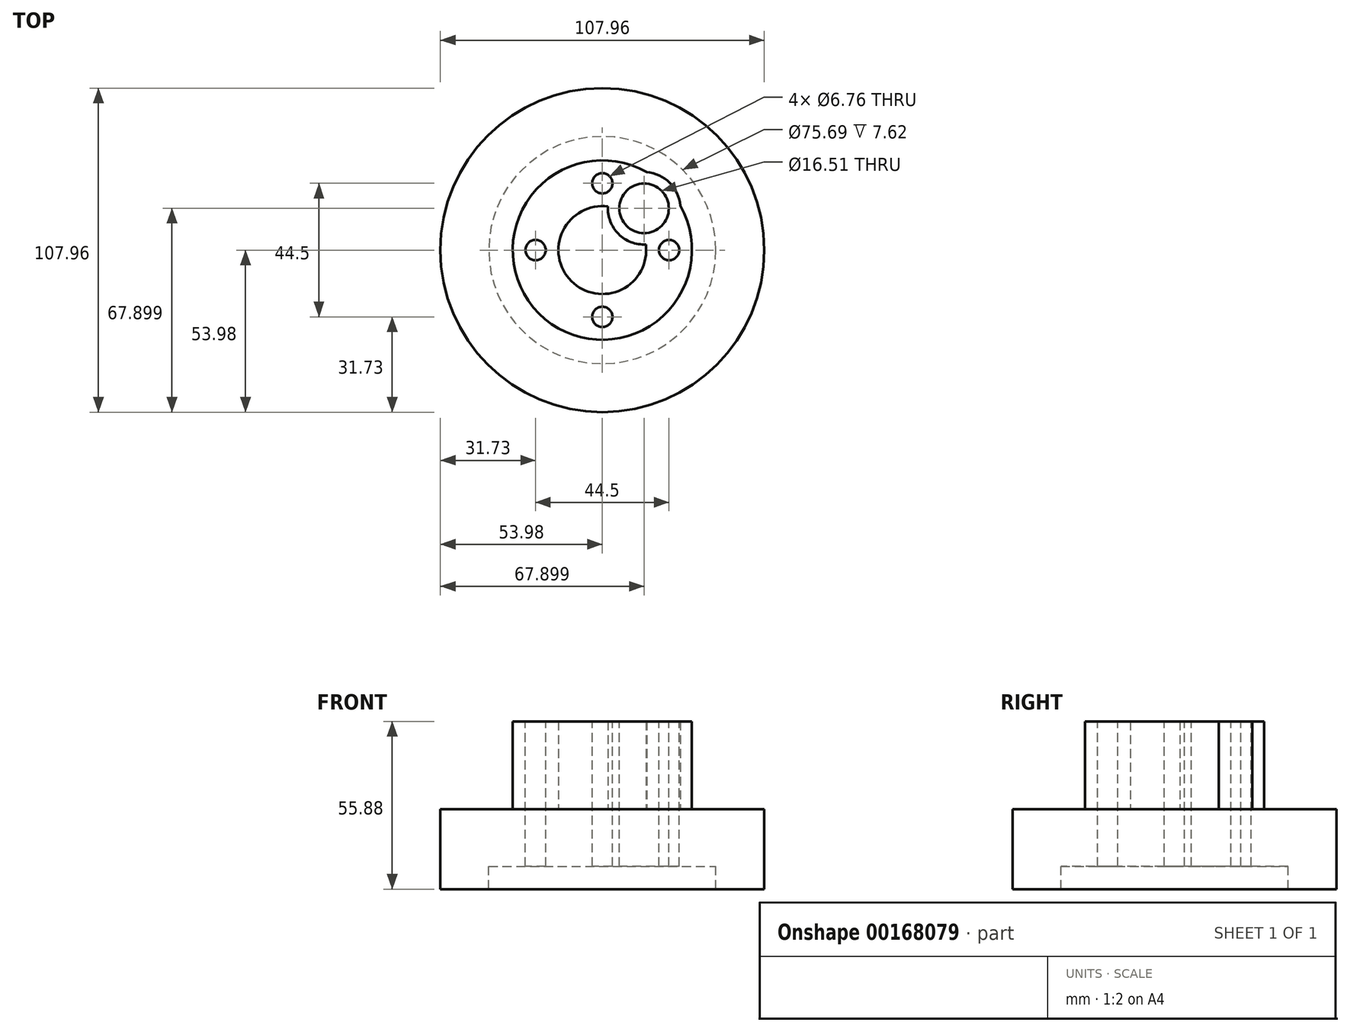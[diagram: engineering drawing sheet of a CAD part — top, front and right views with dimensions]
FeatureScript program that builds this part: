
annotation { "Feature Type Name" : "Feature", "Feature Type Description" : "" }
export const myFeature = defineFeature(function(context is Context, id is Id, definition is map)
    precondition{}
    {
        {
            var Q0;
            Q0=qCreatedBy(makeId("Top.planeOp"),FACE);
            var sketch = newSketch(context, id + "F0", { "sketchPlane" : qUnion([Q0])});
            skCircle(sketch, "E0", {"center": v(0, 0) * mm, "radius": 53.98 * mm});
            skSolve(sketch);
        }
        {
            var Q0;
            Q0=qSketchRegion(id+"F0",true);
            extrude(context, id + "F1", {"entities" : qUnion([Q0]), "depth" : 19.05 * mm});
        }
        {
            var Q0;
            Q0=makeQuery(id+"F1.opExtrude","CAP_FACE",FACE,{"disambiguationData":[OSD([sQuery(id+"F0.wireOp",EDGE,"E0")])],"isStart":false});
            var sketch = newSketch(context, id + "F2", { "sketchPlane" : qUnion([Q0])});
            skCircle(sketch, "E1", {"center": v(0, 0) * mm, "radius": 22.25 * mm, "construction": true});
            skCircle(sketch, "E2", {"center": v(0, 0) * mm, "radius": 14.63 * mm});
            skCircle(sketch, "E3", {"center": v(0, 0) * mm, "radius": 29.87 * mm});
            skSolve(sketch);
        }
        {
            var Q0;
            Q0=qSketchRegion(id+"F2",true);
            var Q1;
            Q1=qConstructionFilter(qBodyType(qCreatedBy(id+"F2",EDGE),BodyType.WIRE),ConstructionObject.NO);
            extrude(context, id + "F3", {"entities" : qUnion([Q0]), "operationType" : NewBodyOperationType.ADD, "surfaceEntities" : qUnion([Q1]), "depth" : 29.2 * mm});
        }
        {
            var Q0;
            Q0=makeQuery(id+"F3.opExtrude","CAP_FACE",FACE,{"disambiguationData":[OSD([sQuery(id+"F2.wireOp",EDGE,"E2"),sQuery(id+"F2.wireOp",EDGE,"E3")])],"isStart":false});
            var sketch = newSketch(context, id + "F4", { "sketchPlane" : qUnion([Q0])});
            skPoint(sketch, "E4", {"position": v(0, -22.25) * mm});
            skPoint(sketch, "E5", {"position": v(-22.25, 0) * mm});
            skPoint(sketch, "E6", {"position": v(0, 22.25) * mm});
            skPoint(sketch, "E7", {"position": v(22.25, 0) * mm});
            skLineSegment(sketch, "E8", {"start": v(-14.63, 0) * mm, "end": v(-29.87, 0) * mm, "construction": true});
            skLineSegment(sketch, "E9", {"start": v(0, -14.63) * mm, "end": v(0, -29.87) * mm, "construction": true});
            skLineSegment(sketch, "E10", {"start": v(14.63, 0) * mm, "end": v(29.87, 0) * mm, "construction": true});
            skLineSegment(sketch, "E11", {"start": v(0, 14.63) * mm, "end": v(0, 29.87) * mm, "construction": true});
            skSolve(sketch);
        }
        {
            var Q0;
            Q0=sQuery(id+"F4.wireOp",VERTEX,"E4");
            var Q1;
            Q1=sQuery(id+"F4.wireOp",VERTEX,"E5");
            var Q2;
            Q2=sQuery(id+"F4.wireOp",VERTEX,"E6");
            var Q3;
            Q3=sQuery(id+"F4.wireOp",VERTEX,"E7");
            var Q4;
            Q4=makeQuery(id+"F1.opExtrude","SWEPT_BODY",BODY,{"disambiguationData":[OSD([sQuery(id+"F0.wireOp",EDGE,"E0")])]});
            hole(context, id + "F5", {"style" : HoleStyle.SIMPLE, "endStyle" : HoleEndStyle.THROUGH, "standardTappedOrClearance" : lookupTablePath({ "standard" : "ANSI", "fit" : "Normal (ASME)", "size" : "1/4", "type" : "Clearance" }), "standardBlindInLast" : lookupTablePath({ "fit" : "Free", "standard" : "ANSI", "size" : "1/4", "type" : "Clearance" }), "holeDiameter" : 6.76 * mm, "locations" : qUnion([Q0, Q1, Q2, Q3]), "scope" : qUnion([Q4]), "isTappedThrough" : true});
        }
        {
            var Q0;
            Q0=makeQuery(id+"F1.opExtrude","CAP_FACE",FACE,{"disambiguationData":[OSD([sQuery(id+"F0.wireOp",EDGE,"E0")])],"isStart":true});
            var sketch = newSketch(context, id + "F6", { "sketchPlane" : qUnion([Q0])});
            skCircle(sketch, "E12", {"center": v(0, 0) * mm, "radius": 37.85 * mm});
            skCircle(sketch, "E13", {"center": v(0, 0) * mm, "radius": 53.98 * mm});
            skSolve(sketch);
        }
        {
            var Q0;
            Q0=qSketchRegion(id+"F6",true);
            extrude(context, id + "F7", {"entities" : qUnion([Q0]), "operationType" : NewBodyOperationType.ADD, "depth" : 7.62 * mm});
        }
        {
            var Q0;
            {var subQ0=sQuery(id+"F0.wireOp",EDGE,"E0");Q0=makeQuery(id+"F3.boolean.opBoolean","SPLIT",FACE,{"disambiguationData":[TD([makeQuery(id+"F1.opExtrude","SWEPT_FACE",FACE,{"disambiguationData":[OSD([subQ0])]})])],"derivedFrom":makeQuery(id+"F1.opExtrude","CAP_FACE",FACE,{"disambiguationData":[OSD([subQ0])],"isStart":false})});}
            var sketch = newSketch(context, id + "F8", { "sketchPlane" : qUnion([Q0])});
            skCircle(sketch, "E14", {"center": v(13.92, 13.92) * mm, "radius": 12.07 * mm});
            skCircle(sketch, "E15.0", {"center": v(22.25, 0) * mm, "radius": 3.38 * mm, "construction": true});
            skCircle(sketch, "E15.1", {"center": v(0, 22.25) * mm, "radius": 3.38 * mm, "construction": true});
            skLineSegment(sketch, "E16", {"start": v(22.25, 0) * mm, "end": v(0, 22.25) * mm, "construction": true});
            skLineSegment(sketch, "E17", {"start": v(0, 0) * mm, "end": v(11.12, 11.12) * mm, "construction": true});
            skLineSegment(sketch, "E18", {"start": v(11.12, 11.12) * mm, "end": v(13.92, 13.92) * mm, "construction": true});
            skSolve(sketch);
        }
        {
            var Q0;
            Q0=qSketchRegion(id+"F8",true);
            var Q1;
            Q1=makeQuery(id+"F3.opExtrude","CAP_FACE",FACE,{"disambiguationData":[OSD([sQuery(id+"F2.wireOp",EDGE,"E2"),sQuery(id+"F2.wireOp",EDGE,"E3")])],"isStart":false});
            extrude(context, id + "F9", {"entities" : qUnion([Q0]), "operationType" : NewBodyOperationType.ADD, "endBound" : BoundingType.UP_TO_SURFACE, "endBoundEntityFace" : qUnion([Q1]), "depth" : 25.4 * mm});
        }
        {
            var Q0;
            Q0=makeQuery(id+"F9.boolean.opBoolean","MERGE",FACE,{"derivedFrom":[makeQuery(id+"F3.opExtrude","CAP_FACE",FACE,{"disambiguationData":[OSD([sQuery(id+"F2.wireOp",EDGE,"E2"),sQuery(id+"F2.wireOp",EDGE,"E3")])],"isStart":false}),makeQuery(id+"F9.opExtrude","CAP_FACE",FACE,{"disambiguationData":[OSD([sQuery(id+"F8.wireOp",EDGE,"E14")])],"isStart":false})]});
            var sketch = newSketch(context, id + "F10", { "sketchPlane" : qUnion([Q0])});
            skPoint(sketch, "E19", {"position": v(13.92, 13.92) * mm});
            skCircle(sketch, "E20", {"center": v(13.92, 13.92) * mm, "radius": 8.26 * mm});
            skSolve(sketch);
        }
        {
            var Q0;
            Q0=qSketchRegion(id+"F10",true);
            extrude(context, id + "F11", {"entities" : qUnion([Q0]), "operationType" : NewBodyOperationType.REMOVE, "endBound" : BoundingType.THROUGH_ALL, "oppositeDirection" : true, "depth" : 25.4 * mm});
        }
    });
